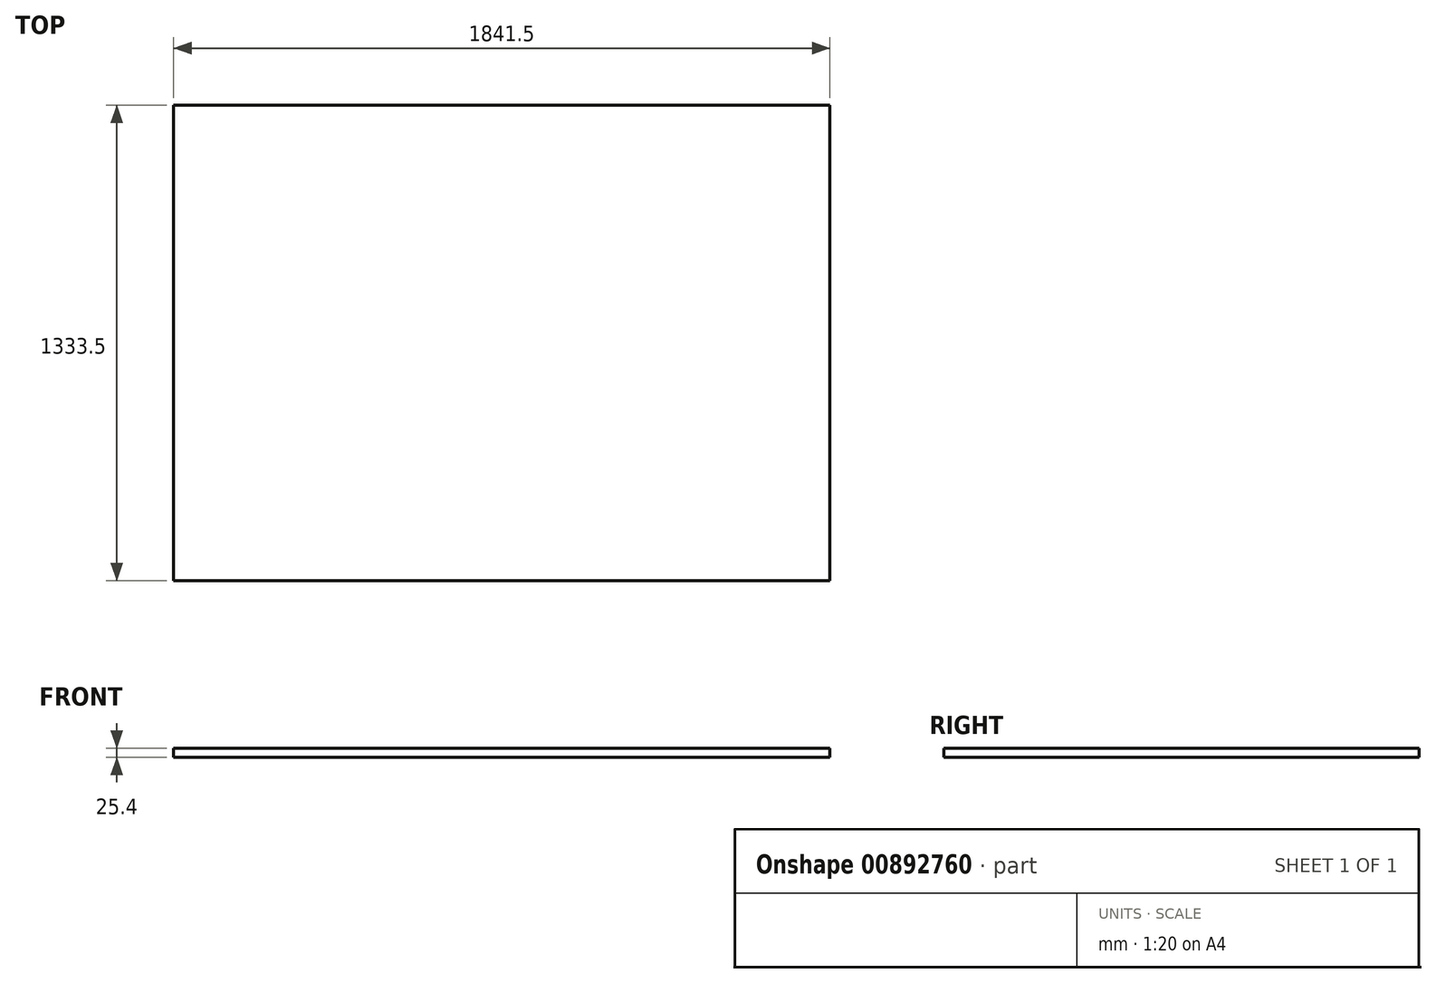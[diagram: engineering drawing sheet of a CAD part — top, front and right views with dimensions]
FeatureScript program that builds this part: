
annotation { "Feature Type Name" : "Feature", "Feature Type Description" : "" }
export const myFeature = defineFeature(function(context is Context, id is Id, definition is map)
    precondition{}
    {
        {
            var Q0;
            Q0=qCreatedBy(makeId("Top.planeOp"),FACE);
            var sketch = newSketch(context, id + "F0", { "sketchPlane" : qUnion([Q0])});
            skLineSegment(sketch, "E0.bottom", {"start": v(-916.3, -666.75) * mm, "end": v(925.2, -666.75) * mm});
            skLineSegment(sketch, "E0.top", {"start": v(-916.3, 666.75) * mm, "end": v(925.2, 666.75) * mm});
            skLineSegment(sketch, "E0.left", {"start": v(-916.3, -666.75) * mm, "end": v(-916.3, 666.75) * mm});
            skLineSegment(sketch, "E0.right", {"start": v(925.2, -666.75) * mm, "end": v(925.2, 666.75) * mm});
            skPoint(sketch, "E0.middle", {"position": v(4.45, 0) * mm});
            skSolve(sketch);
        }
        {
            var Q0;
            Q0 = qSketchRegion(id + "F0", true);
            extrude(context, id + "F1", {"entities" : qUnion([Q0]), "depth" : 25.4 * mm, "offsetDistance" : 25.4 * mm});
        }
    });
